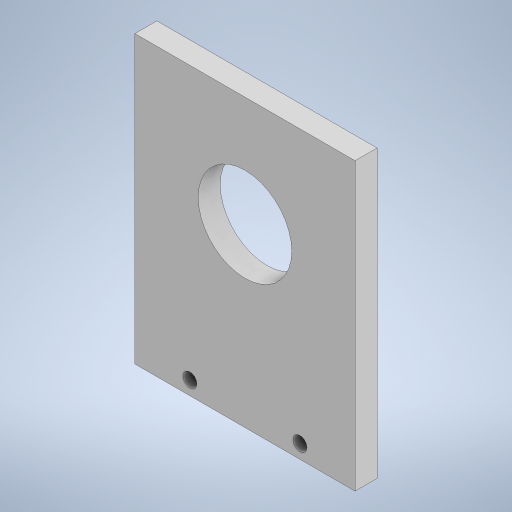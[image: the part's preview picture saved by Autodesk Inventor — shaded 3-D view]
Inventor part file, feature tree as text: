
AUTODESK INVENTOR PART (.ipt)
format: ipt  version: 2024 (Build 280153000, 153)  size: 230,400 bytes
history: native  units: in
note: dims shown in document units (in); Inventor stores cm internally (conversion verified against a paired STEP export)
features: extrude x3, sketch x3
ambient origin geometry x8: Origin, YZ Plane, XZ Plane, XY Plane, X Axis, Y Axis, Z Axis, Center Point
bodies: Solid1 (feature_tree)
feature tree (6):
  extrude  "Extrusion1"  Depth=10.2362in
  extrude  "Extrusion2"  Depth=0.7874in
  extrude  "Extrusion3"  Depth=0.7874in
  sketch  "Sketch1"  dims[d0=7.874in d1=10.2362in]
  sketch  "Sketch2"  dims[d2=0.7874in d3=0.0in d4=3.3465in]
  sketch  "Sketch3"  dims[d5=3.937in d6=3.937in d7=0.7874in d8=0.0in d9=0.5in d10=0.5in d11=0.4921in d12=0.4921in d13=1.9685in d14=1.9685in d15=0.7874in d16=0.0in]
